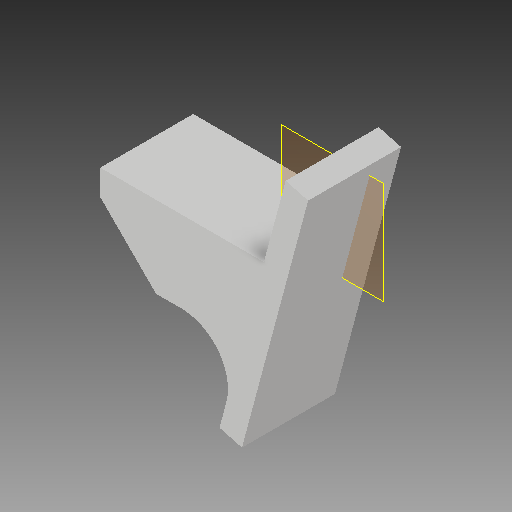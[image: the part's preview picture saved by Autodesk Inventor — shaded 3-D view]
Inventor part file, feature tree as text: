
AUTODESK INVENTOR PART (.ipt)
format: ipt  version: 2018 (Build 220112000, 112)  size: 122,368 bytes
history: native  units: mm
features: plane x3, other x3, sketch x1, extrude x1, fillet x1, chamfer x1, reference x1
ambient origin geometry x8: Origin, YZ Plane, XZ Plane, XY Plane, X Axis, Y Axis, Z Axis, Center Point
bodies: Solid1 (feature_tree)
feature tree (11):
  sketch  "Sketch1"  dims[d0=40.0mm d1=105.0deg d2=5.0mm d3=15.0mm d5=5.0mm d6=3.0mm d7=11.490025mm d9=20.0mm d10=0.0mm d20=17.5mm d21=35.19348mm d22=30.504369mm d23=10.0mm d24=12.0mm d25=2.0mm d26=45.0deg]
  plane  "Work Plane1"
  extrude  "Extrusion1"  TaperAngle=105.0deg  [1 undecoded]
  plane  "Work Plane6"
  plane  "Work Plane3"
  fillet  "Fillet2"  Radius=5.0mm
  chamfer  "Chamfer1"  Distance=15.0mm
  reference  "Reference4"
  other  "<userpath>\Dropbox\Skola\Projekt\Kretsn_Brillz_V2\3D\IR_Transmitter.iam"
  other  "IR_Transmitter.iam"
  other  "Powerbank:1"
note: 1 required parameter value undecoded (feature->parameter linkage not recoverable at this tier; creation-order binding heuristic only, values carry confidence <= 0.55)
